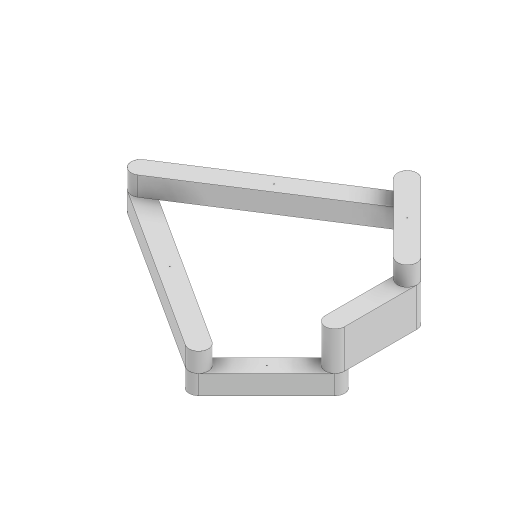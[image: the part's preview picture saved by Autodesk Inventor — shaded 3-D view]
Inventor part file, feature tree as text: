
AUTODESK INVENTOR PART (.ipt)
format: ipt  version: 2024.2 (Build 282272000, 272)  size: 175,616 bytes
history: native  units: mm
features: extrude x7, sketch x1
ambient origin geometry x8: Origin, YZ Plane, XZ Plane, XY Plane, X Axis, Y Axis, Z Axis, Center Point
bodies: Solid7 (feature_tree), Solid8 (feature_tree), Solid9 (feature_tree), Solid10 (feature_tree)
feature tree (8):
  sketch  "Sketch1"  dims[d42=1000.0mm d43=1000.0mm d45=75.0mm d46=20.0mm d47=20.0mm d48=20.0mm d49=20.0mm d50=20.0mm d51=100.0mm d52=100.0mm d53=200.0mm d54=200.0mm d55=45.0deg d56=45.0deg d57=20.0mm d58=0.0mm d59=20.0mm d60=0.0mm d61=40.0mm d62=0.0mm d63=60.0mm d64=0.0mm d65=20.0mm d66=0.0mm d67=40.0mm d68=0.0mm d69=40.0mm d70=0.0mm d71=21.424855mm d72=9.991072mm d73=154.809503mm d74=54.105339mm d75=35.355339mm d76=72.855339mm d77=13.570873mm d78=37.5mm d79=35.36mm d80=1.0mm]
  extrude  "Extrusion6"  Depth=37.5mm
  extrude  "Extrusion7"  Depth=37.5mm
  extrude  "Extrusion8"  Depth=20.0mm
  extrude  "Extrusion9"  Depth=20.0mm
  extrude  "Extrusion10"  Depth=20.0mm
  extrude  "Extrusion11"  Depth=20.0mm
  extrude  "Extrusion12"  Depth=20.0mm
